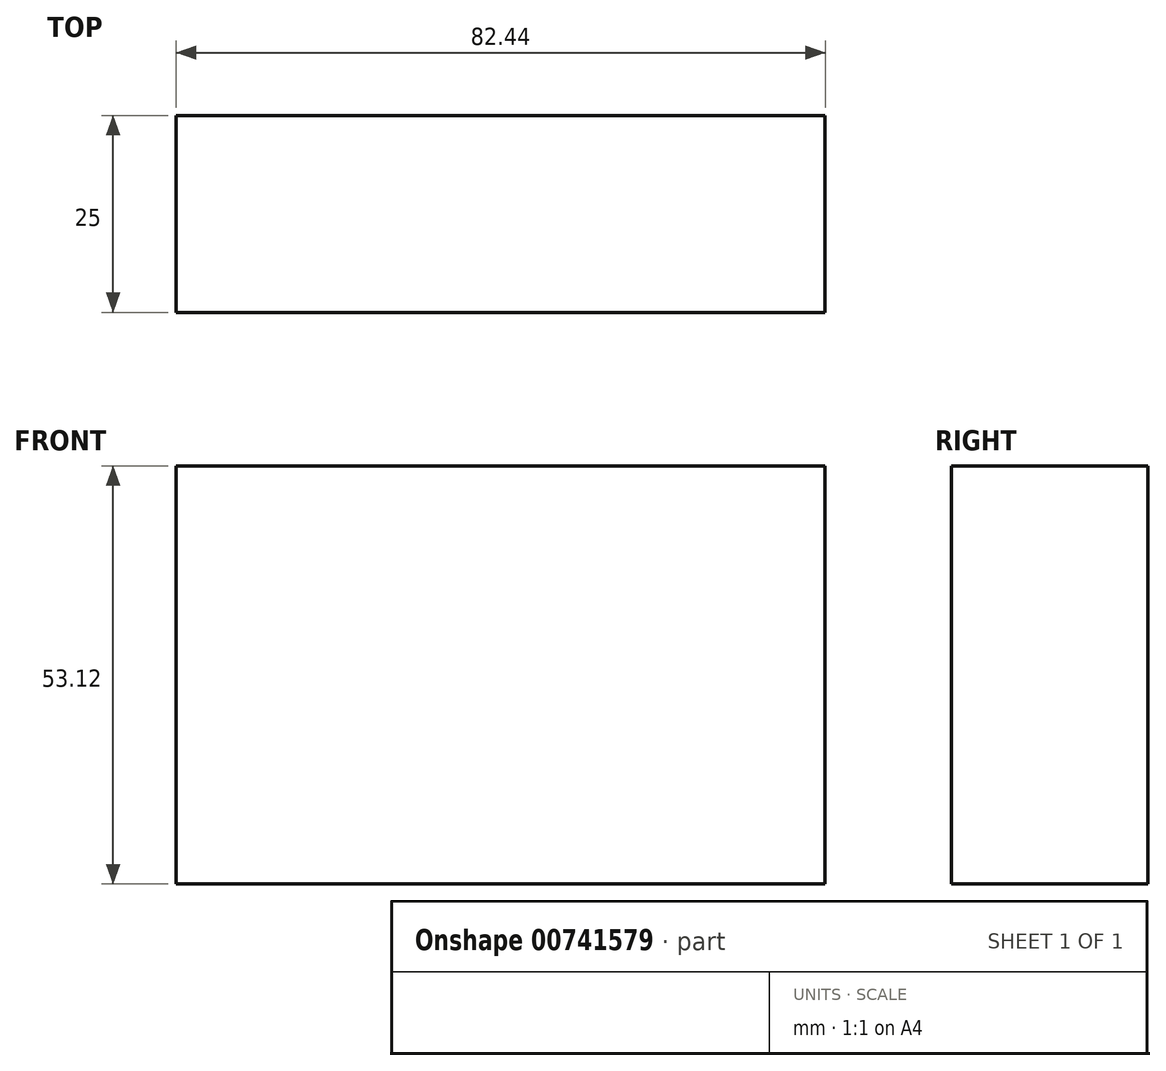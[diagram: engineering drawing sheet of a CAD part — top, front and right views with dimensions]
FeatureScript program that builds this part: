
annotation { "Feature Type Name" : "Feature", "Feature Type Description" : "" }
export const myFeature = defineFeature(function(context is Context, id is Id, definition is map)
    precondition{}
    {
        {
            var Q0;
            Q0=qCreatedBy(makeId("Front.planeOp"),FACE);
            var sketch = newSketch(context, id + "F0", { "sketchPlane" : qUnion([Q0])});
            skLineSegment(sketch, "E0.bottom", {"start": v(-162.44, 21.1) * mm, "end": v(-80, 21.1) * mm});
            skLineSegment(sketch, "E0.top", {"start": v(-162.44, -32.02) * mm, "end": v(-80, -32.02) * mm});
            skLineSegment(sketch, "E0.left", {"start": v(-162.44, 21.1) * mm, "end": v(-162.44, -32.02) * mm});
            skLineSegment(sketch, "E0.right", {"start": v(-80, 21.1) * mm, "end": v(-80, -32.02) * mm});
            skSolve(sketch);
        }
        {
            var Q0;
            Q0=makeQuery(id+"F0.imprint","IMPRINT",FACE,{"disambiguationData":[TD([[makeQuery(id+"F0.imprint","IMPRINT",EDGE,{"derivedFrom":sQuery(id+"F0.wireOp",EDGE,"E0.bottom")}),-1.0]])]});
            extrude(context, id + "F1", {"entities" : qUnion([Q0]), "depth" : 25 * mm, "offsetDistance" : 25 * mm});
        }
    });
